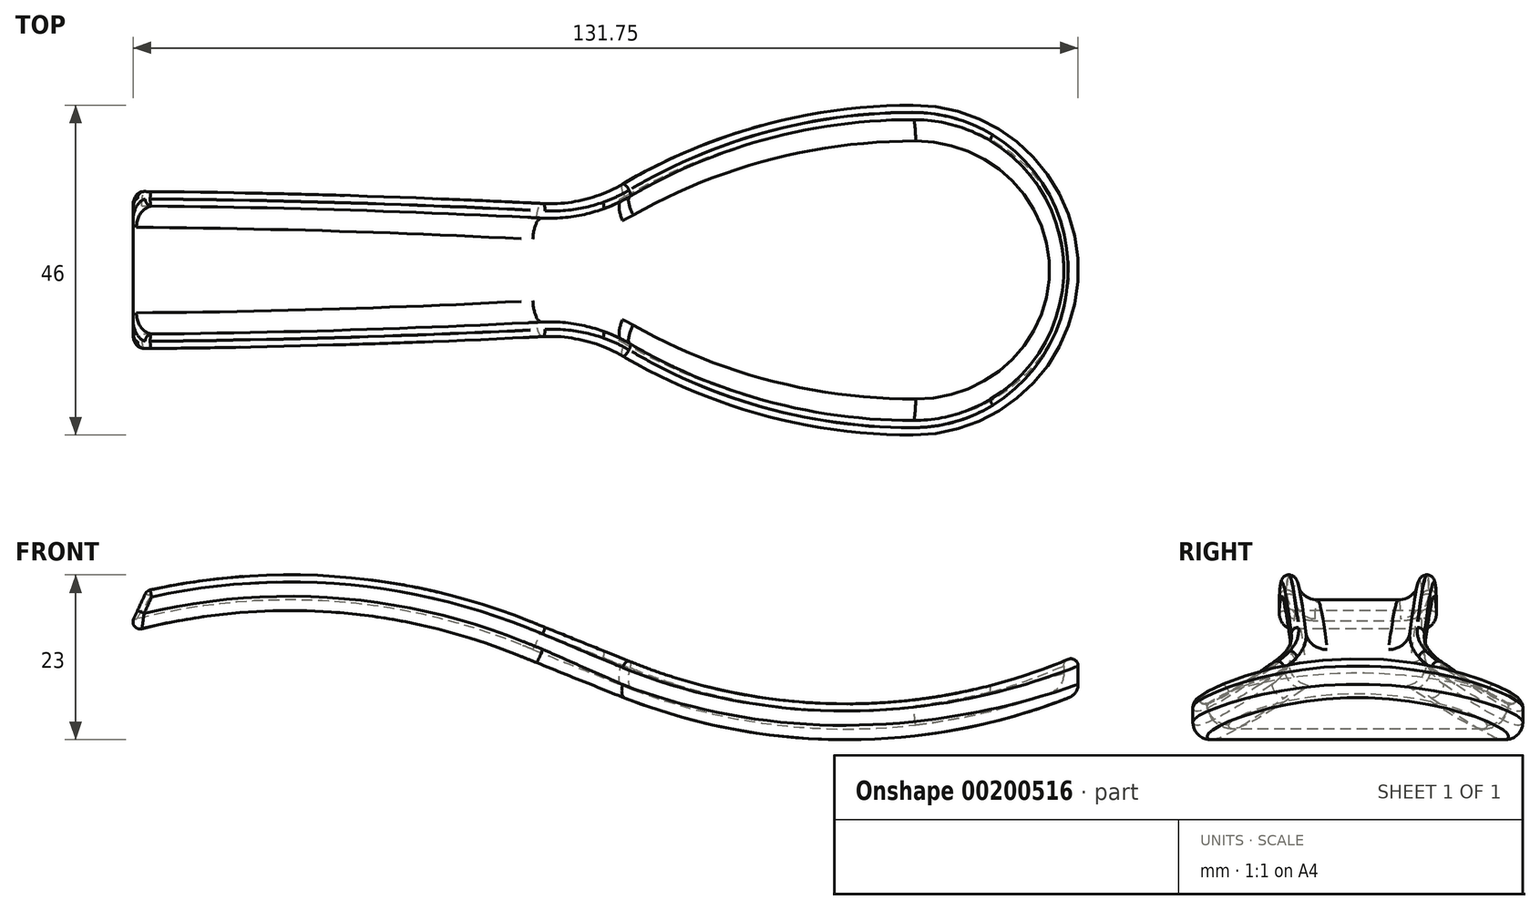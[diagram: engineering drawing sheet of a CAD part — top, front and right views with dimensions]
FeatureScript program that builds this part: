
annotation { "Feature Type Name" : "Feature", "Feature Type Description" : "" }
export const myFeature = defineFeature(function(context is Context, id is Id, definition is map)
    precondition{}
    {
        {
            var Q0;
            Q0=qCreatedBy(makeId("Front.planeOp"),FACE);
            var sketch = newSketch(context, id + "F0", { "sketchPlane" : qUnion([Q0])});
            skArc(sketch, "E0", {"start": v(63.5, 0) * mm, "mid": v(33.31, 6.14) * mm, "end": v(2.92, 1.11) * mm});
            skLineSegment(sketch, "E1", {"start": v(63.5, 0) * mm, "end": v(77.64, -5.7) * mm});
            skArc(sketch, "E2", {"start": v(77.64, -5.7) * mm, "mid": v(109.4, -11.85) * mm, "end": v(141.14, -5.7) * mm});
            skLineSegment(sketch, "E3", {"start": v(0, 0) * mm, "end": v(63.5, 0) * mm, "construction": true});
            skLineSegment(sketch, "E4", {"start": v(77.64, -5.7) * mm, "end": v(141.14, -5.7) * mm, "construction": true});
            skLineSegment(sketch, "E5", {"start": v(0, 6.15) * mm, "end": v(141.14, 6.15) * mm, "construction": true});
            skLineSegment(sketch, "E6", {"start": v(141.14, -11.85) * mm, "end": v(-4.3, -11.85) * mm, "construction": true});
            skLineSegment(sketch, "E7", {"start": v(141.14, -11.85) * mm, "end": v(141.14, 6.15) * mm, "construction": true});
            skLineSegment(sketch, "E8", {"start": v(0, 6.15) * mm, "end": v(0, -11.85) * mm, "construction": true});
            skArc(sketch, "E9", {"start": v(-1.11, -5) * mm, "mid": v(-0.62, -3.79) * mm, "end": v(-0.27, -2.53) * mm});
            skPoint(sketch, "E10.visualSharp", {"position": v(0, 0) * mm});
            skArc(sketch, "E10.filletArc", {"start": v(2.92, 1.11) * mm, "mid": v(0.85, -0.3) * mm, "end": v(-0.27, -2.53) * mm});
            skLineSegment(sketch, "E11", {"start": v(-1.11, -5) * mm, "end": v(-4.3, -11.85) * mm});
            skSolve(sketch);
        }
        {
            var Q0;
            Q0=sQuery(id+"F0.wireOp",EDGE,"E11");
            var Q1;
            Q1=sQuery(id+"F0.wireOp",VERTEX,"E11.end");
            cPlane(context, id + "F1", {"entities" : qUnion([Q0, Q1]), "cplaneType" : CPlaneType.LINE_POINT, "offset" : 25 * mm, "width" : 150 * mm, "height" : 150 * mm});
        }
        {
            var Q0;
            Q0=qCreatedBy(id+"F1.planeOp",FACE);
            var sketch = newSketch(context, id + "F2", { "sketchPlane" : qUnion([Q0])});
            skLineSegment(sketch, "E12.bottom", {"start": v(2.61, 30) * mm, "end": v(-0.39, 30) * mm});
            skLineSegment(sketch, "E12.top", {"start": v(2.61, -30) * mm, "end": v(-0.39, -30) * mm});
            skLineSegment(sketch, "E12.left", {"start": v(2.61, 30) * mm, "end": v(2.61, -30) * mm});
            skLineSegment(sketch, "E12.right", {"start": v(-0.39, 30) * mm, "end": v(-0.39, -30) * mm});
            skPoint(sketch, "E12.middle", {"position": v(1.11, 0) * mm});
            skSolve(sketch);
        }
        {
            var Q0;
            Q0 = qSketchRegion(id + "F2", true);
            var Q1;
            Q1=sQuery(id+"F0.wireOp",EDGE,"E11");
            var Q2;
            Q2=sQuery(id+"F0.wireOp",EDGE,"E9");
            var Q3;
            Q3=sQuery(id+"F0.wireOp",EDGE,"E10.filletArc");
            var Q4;
            Q4=sQuery(id+"F0.wireOp",EDGE,"E0");
            var Q5;
            Q5=sQuery(id+"F0.wireOp",EDGE,"E1");
            var Q6;
            Q6=sQuery(id+"F0.wireOp",EDGE,"E2");
            var Q7;
            Q7=sQuery(id+"F0.wireOp",EDGE,"1WxR1Lvr-zJyr-FBdt-gofM-uj7Kzw3sXY7P");
            var Q8;
            Q8=sQuery(id+"F0.wireOp",EDGE,"ToBQ2O02-yujo-ZkVP-JNpa-i62q8QJA0fiL");
            sweep(context, id + "F3", {"profiles" : qUnion([Q0]), "path" : qUnion([Q1, Q2, Q3, Q4, Q5, Q6, Q7, Q8])});
        }
        {
            var Q0;
            Q0=qCreatedBy(makeId("Top.planeOp"),FACE);
            var sketch = newSketch(context, id + "F4", { "sketchPlane" : qUnion([Q0])});
            skLineSegment(sketch, "E13", {"start": v(0, 0) * mm, "end": v(141.7, 0) * mm, "construction": true});
            skArc(sketch, "E14", {"start": v(141.7, 0) * mm, "mid": v(134.97, 16.26) * mm, "end": v(118.7, 23) * mm});
            skArc(sketch, "E15", {"start": v(118.7, 23) * mm, "mid": v(97.73, 20.2) * mm, "end": v(78.22, 12) * mm});
            skArc(sketch, "E16", {"start": v(67.07, 9.28) * mm, "mid": v(72.84, 9.82) * mm, "end": v(78.22, 12) * mm});
            skArc(sketch, "E17", {"start": v(67.07, 9.28) * mm, "mid": v(34.45, 10.55) * mm, "end": v(1.82, 11) * mm});
            skLineSegment(sketch, "E18", {"start": v(76.56, 11) * mm, "end": v(-5.66, 11) * mm, "construction": true});
            skPoint(sketch, "E19.visualSharp", {"position": v(-5.15, 10.99) * mm});
            skArc(sketch, "E20.MirrorCS", {"start": v(67.07, -9.28) * mm, "mid": v(34.45, -10.55) * mm, "end": v(1.82, -11) * mm});
            skArc(sketch, "E21.MirrorCS", {"start": v(67.07, -9.28) * mm, "mid": v(72.84, -9.82) * mm, "end": v(78.22, -12) * mm});
            skArc(sketch, "E22.MirrorCS", {"start": v(118.7, -23) * mm, "mid": v(97.73, -20.2) * mm, "end": v(78.22, -12) * mm});
            skArc(sketch, "E23.MirrorCS", {"start": v(141.7, 0) * mm, "mid": v(134.97, -16.26) * mm, "end": v(118.7, -23) * mm});
            skPoint(sketch, "E24.MirrorP", {"position": v(-5.15, -10.99) * mm});
            skLineSegment(sketch, "E25.bottom", {"start": v(160.85, -37.5) * mm, "end": v(-19.15, -37.5) * mm});
            skLineSegment(sketch, "E25.top", {"start": v(160.85, 37.5) * mm, "end": v(-19.15, 37.5) * mm});
            skLineSegment(sketch, "E25.left", {"start": v(160.85, -37.5) * mm, "end": v(160.85, 37.5) * mm});
            skLineSegment(sketch, "E25.right", {"start": v(-19.15, -37.5) * mm, "end": v(-19.15, 37.5) * mm});
            skPoint(sketch, "E25.middle", {"position": v(70.85, 0) * mm});
            skPoint(sketch, "E26", {"position": v(160.85, 0) * mm});
            skPoint(sketch, "E27", {"position": v(-19.15, 0) * mm});
            skArc(sketch, "E28", {"start": v(-1.74, 9.52) * mm, "mid": v(-5.66, 0) * mm, "end": v(-1.74, -9.52) * mm});
            skPoint(sketch, "E29.visualSharp", {"position": v(0, 11) * mm});
            skArc(sketch, "E29.filletArc", {"start": v(1.82, 11) * mm, "mid": v(-0.1, 10.62) * mm, "end": v(-1.74, 9.52) * mm});
            skPoint(sketch, "E30.visualSharp", {"position": v(0, -11) * mm});
            skArc(sketch, "E30.filletArc", {"start": v(-1.74, -9.52) * mm, "mid": v(-0.1, -10.62) * mm, "end": v(1.82, -11) * mm});
            skSolve(sketch);
        }
        {
            var Q0;
            Q0 = qSketchRegion(id + "F4", true);
            extrude(context, id + "F5", {"entities" : qUnion([Q0]), "operationType" : NewBodyOperationType.REMOVE, "endBound" : BoundingType.THROUGH_ALL, "oppositeDirection" : true, "depth" : 25 * mm, "hasSecondDirection" : true, "secondDirectionBound" : SecondDirectionBoundingType.THROUGH_ALL, "secondDirectionOppositeDirection" : false, "secondDirectionDepth" : 25 * mm});
        }
        {
            var Q0;
            Q0=qCreatedBy(makeId("Top.planeOp"),FACE);
            var sketch = newSketch(context, id + "F6", { "sketchPlane" : qUnion([Q0])});
            skArc(sketch, "E31.1", {"start": v(141.7, 0) * mm, "mid": v(134.97, 16.26) * mm, "end": v(118.7, 23) * mm});
            skArc(sketch, "E31.2", {"start": v(118.7, 23) * mm, "mid": v(97.73, 20.2) * mm, "end": v(78.22, 12) * mm});
            skArc(sketch, "E31.3", {"start": v(67.07, 9.28) * mm, "mid": v(72.84, 9.82) * mm, "end": v(78.22, 12) * mm});
            skArc(sketch, "E31.4", {"start": v(67.07, 9.28) * mm, "mid": v(34.45, 10.55) * mm, "end": v(1.82, 11) * mm});
            skPoint(sketch, "E31.6", {"position": v(-5.15, 10.99) * mm});
            skArc(sketch, "E31.7", {"start": v(67.07, -9.28) * mm, "mid": v(34.45, -10.55) * mm, "end": v(1.82, -11) * mm});
            skArc(sketch, "E31.8", {"start": v(67.07, -9.28) * mm, "mid": v(72.84, -9.82) * mm, "end": v(78.22, -12) * mm});
            skArc(sketch, "E31.9", {"start": v(118.7, -23) * mm, "mid": v(97.73, -20.2) * mm, "end": v(78.22, -12) * mm});
            skArc(sketch, "E31.10", {"start": v(141.7, 0) * mm, "mid": v(134.97, -16.26) * mm, "end": v(118.7, -23) * mm});
            skPoint(sketch, "E31.11", {"position": v(-5.15, -10.99) * mm});
            skLineSegment(sketch, "E31.15", {"start": v(-19.15, -37.5) * mm, "end": v(-19.15, 37.5) * mm});
            skPoint(sketch, "E31.16", {"position": v(70.85, 0) * mm});
            skPoint(sketch, "E31.18", {"position": v(-19.15, 0) * mm});
            skArc(sketch, "E31.19", {"start": v(-1.74, 9.52) * mm, "mid": v(-5.66, 0) * mm, "end": v(-1.74, -9.52) * mm});
            skPoint(sketch, "E31.20", {"position": v(0, 11) * mm});
            skArc(sketch, "E31.21", {"start": v(1.82, 11) * mm, "mid": v(-0.1, 10.62) * mm, "end": v(-1.74, 9.52) * mm});
            skPoint(sketch, "E31.22", {"position": v(0, -11) * mm});
            skArc(sketch, "E31.23", {"start": v(-1.74, -9.52) * mm, "mid": v(-0.1, -10.62) * mm, "end": v(1.82, -11) * mm});
            skArc(sketch, "E32.0", {"start": v(66.97, 7.28) * mm, "mid": v(33.83, 8.56) * mm, "end": v(0.67, 9) * mm});
            skArc(sketch, "E32.1", {"start": v(66.97, 7.28) * mm, "mid": v(73.32, 7.88) * mm, "end": v(79.23, 10.28) * mm});
            skArc(sketch, "E32.2", {"start": v(0.67, 9) * mm, "mid": v(-3.66, 0) * mm, "end": v(0.67, -9) * mm});
            skArc(sketch, "E32.3", {"start": v(118.7, 21) * mm, "mid": v(98.25, 18.27) * mm, "end": v(79.23, 10.28) * mm});
            skArc(sketch, "E32.4", {"start": v(139.7, 0) * mm, "mid": v(133.55, 14.85) * mm, "end": v(118.7, 21) * mm});
            skArc(sketch, "E32.5", {"start": v(66.97, -7.28) * mm, "mid": v(33.83, -8.56) * mm, "end": v(0.67, -9) * mm});
            skArc(sketch, "E32.6", {"start": v(66.97, -7.28) * mm, "mid": v(73.32, -7.88) * mm, "end": v(79.23, -10.28) * mm});
            skArc(sketch, "E32.7", {"start": v(118.7, -21) * mm, "mid": v(98.25, -18.27) * mm, "end": v(79.23, -10.28) * mm});
            skArc(sketch, "E32.8", {"start": v(139.7, 0) * mm, "mid": v(133.55, -14.85) * mm, "end": v(118.7, -21) * mm});
            skSolve(sketch);
        }
        {
            var Q0;
            Q0 = qSketchRegion(id + "F6", true);
            extrude(context, id + "F7", {"entities" : qUnion([Q0]), "operationType" : NewBodyOperationType.ADD, "depth" : 25 * mm, "hasSecondDirection" : true, "secondDirectionOppositeDirection" : true, "secondDirectionDepth" : 25 * mm});
        }
        {
            var Q0;
            Q0=qCreatedBy(makeId("Front.planeOp"),FACE);
            var sketch = newSketch(context, id + "F8", { "sketchPlane" : qUnion([Q0])});
            skLineSegment(sketch, "E33.0", {"start": v(-5.64, -2.9) * mm, "end": v(-5.66, -2.93) * mm});
            skArc(sketch, "E33.1", {"start": v(-5.64, -2.9) * mm, "mid": v(-5.36, -2.2) * mm, "end": v(-5.16, -1.46) * mm});
            skArc(sketch, "E33.2", {"start": v(79.51, -1.06) * mm, "mid": v(110.71, -6.84) * mm, "end": v(141.7, -0.03) * mm});
            skLineSegment(sketch, "E33.3", {"start": v(65.37, 4.64) * mm, "end": v(79.51, -1.06) * mm});
            skArc(sketch, "E33.4", {"start": v(65.37, 4.64) * mm, "mid": v(33.4, 11.14) * mm, "end": v(1.22, 5.82) * mm});
            skArc(sketch, "E33.5", {"start": v(1.22, 5.82) * mm, "mid": v(-2.9, 3) * mm, "end": v(-5.16, -1.46) * mm});
            skLineSegment(sketch, "E34.0", {"start": v(-1.11, -5) * mm, "end": v(-5.66, -14.76) * mm});
            skArc(sketch, "E34.1", {"start": v(-1.11, -5) * mm, "mid": v(-0.62, -3.79) * mm, "end": v(-0.27, -2.53) * mm});
            skArc(sketch, "E34.2", {"start": v(2.92, 1.11) * mm, "mid": v(0.85, -0.3) * mm, "end": v(-0.27, -2.53) * mm});
            skArc(sketch, "E34.3", {"start": v(63.5, 0) * mm, "mid": v(33.31, 6.14) * mm, "end": v(2.92, 1.11) * mm});
            skLineSegment(sketch, "E34.4", {"start": v(63.5, 0) * mm, "end": v(77.64, -5.7) * mm});
            skArc(sketch, "E34.5", {"start": v(77.64, -5.7) * mm, "mid": v(109.7, -11.85) * mm, "end": v(141.7, -5.47) * mm});
            skLineSegment(sketch, "E35.bottom", {"start": v(141.7, -25) * mm, "end": v(-5.66, -25) * mm});
            skLineSegment(sketch, "E35.top", {"start": v(141.7, 25) * mm, "end": v(-5.66, 25) * mm});
            skLineSegment(sketch, "E35.left", {"start": v(141.7, -25) * mm, "end": v(141.7, -5.47) * mm});
            skLineSegment(sketch, "E35.right", {"start": v(-5.66, -25) * mm, "end": v(-5.66, -14.76) * mm});
            skPoint(sketch, "E35.middle", {"position": v(68.02, 0) * mm});
            skPoint(sketch, "E36.orphan", {"position": v(141.14, -5.7) * mm});
            skPoint(sketch, "E37.orphan", {"position": v(-4.3, -11.85) * mm});
            skLineSegment(sketch, "E38.trimOffspring", {"start": v(-5.66, -2.93) * mm, "end": v(-5.66, 25) * mm});
            skLineSegment(sketch, "E39.trimOffspring", {"start": v(141.7, -0.03) * mm, "end": v(141.7, 25) * mm});
            skSolve(sketch);
        }
        {
            var Q0;
            Q0 = qSketchRegion(id + "F8", true);
            extrude(context, id + "F9", {"entities" : qUnion([Q0]), "operationType" : NewBodyOperationType.REMOVE, "oppositeDirection" : true, "depth" : 25 * mm, "hasSecondDirection" : true, "secondDirectionOppositeDirection" : false, "secondDirectionDepth" : 25 * mm});
        }
        {
            var Q0;
            Q0=makeQuery(id+"F7.boolean.opBoolean","INTERSECT",EDGE,{"derivedFrom":[makeQuery(id+"F3.opSweep","SWEPT_FACE",FACE,{"disambiguationData":[OSD([sQuery(id+"F0.wireOp",EDGE,"E2"),sQuery(id+"F2.wireOp",EDGE,"E12.right")])]}),makeQuery(id+"F7.opExtrude","SWEPT_FACE",FACE,{"disambiguationData":[OSD([sQuery(id+"F6.wireOp",EDGE,"E32.7")])]})]});
            fillet(context, id + "F10", {"entities" : qUnion([Q0]), "radius" : 3 * mm, "tangentPropagation" : true, "allowEdgeOverflow" : false});
        }
        {
            var Q0;
            {var subQ0=makeQuery(id+"F5.opExtrude","SWEPT_FACE",FACE,{"disambiguationData":[OSD([sQuery(id+"F4.wireOp",EDGE,"E14"),sQuery(id+"F4.wireOp",EDGE,"E23.MirrorCS")])]});Q0=makeQuery(id+"F9.boolean.opBoolean","INTERSECT",EDGE,{"derivedFrom":[makeQuery(id+"F7.boolean.opBoolean","MERGE",FACE,{"derivedFrom":[makeQuery(id+"F5.boolean.opBoolean","COPY",FACE,{"disambiguationData":[TD([makeQuery(id+"F5.opExtrude","SWEPT_FACE",FACE,{"disambiguationData":[OSD([sQuery(id+"F4.wireOp",EDGE,"E15")])]})])],"derivedFrom":subQ0}),makeQuery(id+"F5.boolean.opBoolean","COPY",FACE,{"disambiguationData":[TD([makeQuery(id+"F5.opExtrude","SWEPT_FACE",FACE,{"disambiguationData":[OSD([sQuery(id+"F4.wireOp",EDGE,"E22.MirrorCS")])]})])],"derivedFrom":subQ0}),makeQuery(id+"F7.opExtrude","SWEPT_FACE",FACE,{"disambiguationData":[OSD([sQuery(id+"F6.wireOp",EDGE,"E31.1"),sQuery(id+"F6.wireOp",EDGE,"E31.10")])]})]}),makeQuery(id+"F9.opExtrude","SWEPT_FACE",FACE,{"disambiguationData":[OSD([sQuery(id+"F8.wireOp",EDGE,"E34.5")])]})]});}
            fillet(context, id + "F11", {"entities" : qUnion([Q0]), "radius" : 2 * mm, "tangentPropagation" : true, "allowEdgeOverflow" : false});
        }
        {
            var Q0;
            {var subQ1=sQuery(id+"F6.wireOp",EDGE,"E32.5");var subQ3=sQuery(id+"F2.wireOp",EDGE,"E12.right");Q0=makeQuery(id+"F9.boolean.opBoolean","INTERSECT",EDGE,{"derivedFrom":[makeQuery(id+"F7.boolean.opBoolean","SPLIT",FACE,{"disambiguationData":[TD([makeQuery(id+"F3.opSweep","SWEPT_FACE",FACE,{"disambiguationData":[OSD([sQuery(id+"F0.wireOp",EDGE,"E0"),subQ3])]})])],"derivedFrom":makeQuery(id+"F7.opExtrude","SWEPT_FACE",FACE,{"disambiguationData":[OSD([subQ1])]})}),makeQuery(id+"F9.opExtrude","SWEPT_FACE",FACE,{"disambiguationData":[OSD([sQuery(id+"F8.wireOp",EDGE,"E33.4")])]})]});}
            var Q1;
            Q1=makeQuery(id+"F9.boolean.opBoolean","INTERSECT",EDGE,{"derivedFrom":[makeQuery(id+"F7.boolean.opBoolean","MERGE",FACE,{"derivedFrom":[makeQuery(id+"F5.boolean.opBoolean","COPY",FACE,{"derivedFrom":makeQuery(id+"F5.opExtrude","SWEPT_FACE",FACE,{"disambiguationData":[OSD([sQuery(id+"F4.wireOp",EDGE,"E20.MirrorCS")])]})}),makeQuery(id+"F7.opExtrude","SWEPT_FACE",FACE,{"disambiguationData":[OSD([sQuery(id+"F6.wireOp",EDGE,"E31.7")])]})]}),makeQuery(id+"F9.opExtrude","SWEPT_FACE",FACE,{"disambiguationData":[OSD([sQuery(id+"F8.wireOp",EDGE,"E33.4")])]})]});
            fillet(context, id + "F12", {"entities" : qUnion([Q0, Q1]), "radius" : 1 * mm, "tangentPropagation" : true, "allowEdgeOverflow" : false});
        }
        {
            var Q0;
            Q0=qCreatedBy(id+"F1.planeOp",FACE);
            var sketch = newSketch(context, id + "F13", { "sketchPlane" : qUnion([Q0])});
            skLineSegment(sketch, "E40.bottom", {"start": v(6.98, 17.6) * mm, "end": v(-6.98, 17.6) * mm});
            skLineSegment(sketch, "E40.top", {"start": v(6.98, -17.6) * mm, "end": v(-6.98, -17.6) * mm});
            skLineSegment(sketch, "E40.left", {"start": v(6.98, 17.6) * mm, "end": v(6.98, -17.6) * mm});
            skLineSegment(sketch, "E40.right", {"start": v(-6.98, 17.6) * mm, "end": v(-6.98, -17.6) * mm});
            skPoint(sketch, "E40.middle", {"position": v(0, 0) * mm});
            skSolve(sketch);
        }
        {
            var Q0;
            Q0 = qSketchRegion(id + "F13", true);
            extrude(context, id + "F14", {"entities" : qUnion([Q0]), "operationType" : NewBodyOperationType.REMOVE, "oppositeDirection" : true, "depth" : 30 * mm});
        }
        {
            var Q0;
            Q0=makeQuery(id+"F14.boolean.opBoolean","COPY",FACE,{"derivedFrom":makeQuery(id+"F14.opExtrude","SWEPT_FACE",FACE,{"disambiguationData":[OSD([sQuery(id+"F13.wireOp",EDGE,"E40.left")])]})});
            fillet(context, id + "F15", {"entities" : qUnion([Q0]), "radius" : 1 * mm, "tangentPropagation" : true, "allowEdgeOverflow" : false});
        }
    });
